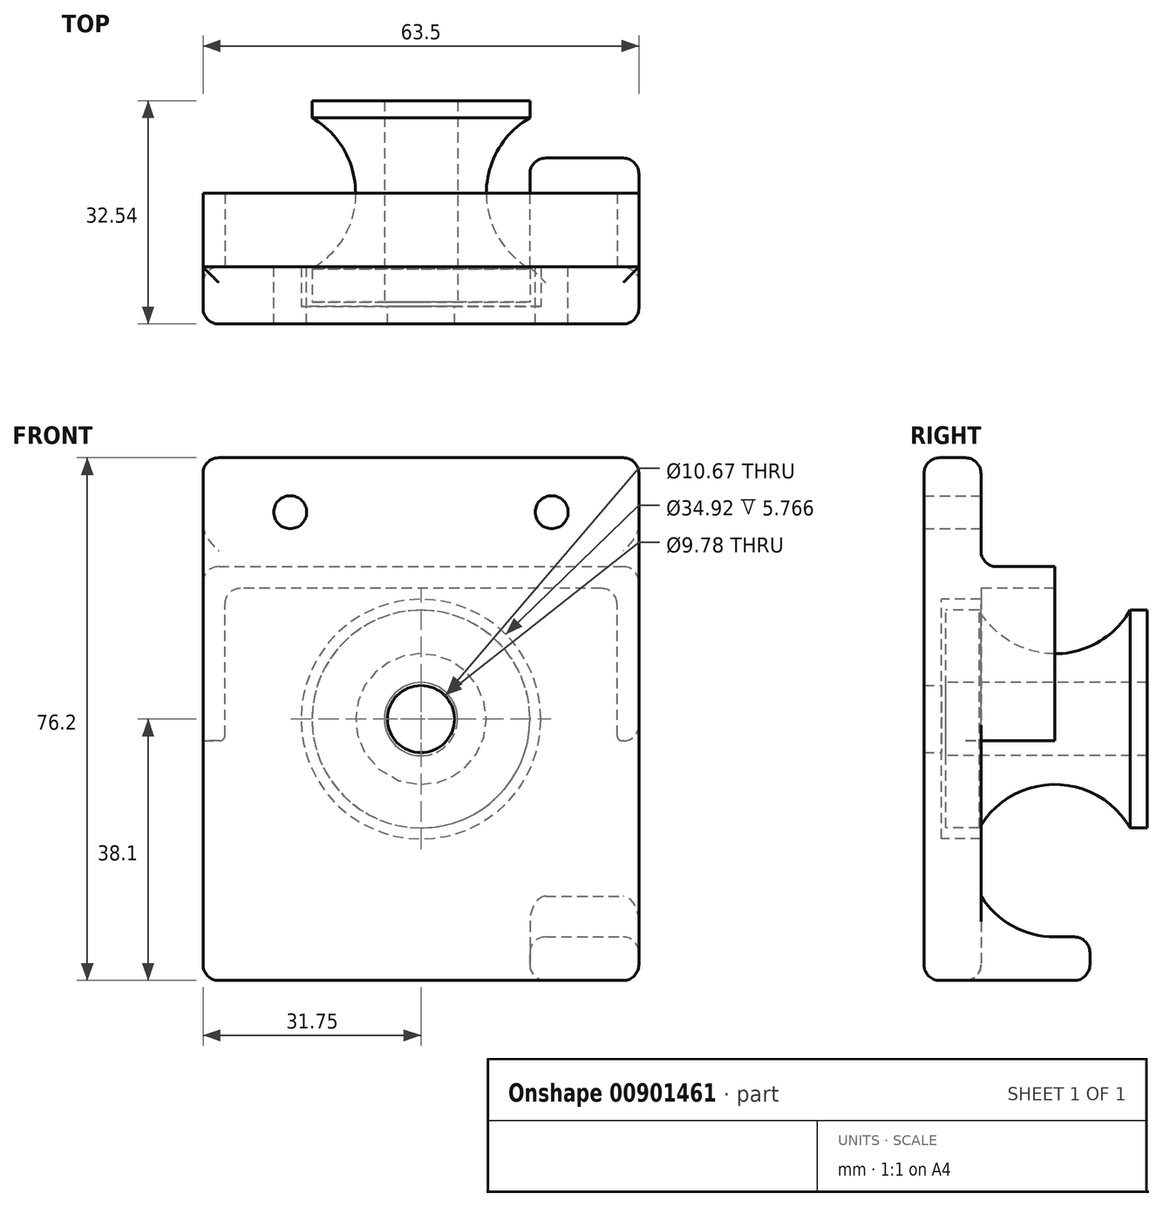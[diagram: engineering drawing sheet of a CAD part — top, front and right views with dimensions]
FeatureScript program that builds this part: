
annotation { "Feature Type Name" : "Feature", "Feature Type Description" : "" }
export const myFeature = defineFeature(function(context is Context, id is Id, definition is map)
    precondition{}
    {
        {
            var Q0;
            Q0=qCreatedBy(makeId("Right.planeOp"),FACE);
            var sketch = newSketch(context, id + "F0", { "sketchPlane" : qUnion([Q0])});
            skLineSegment(sketch, "E0", {"start": v(-15.88, 0) * mm, "end": v(15.88, 0) * mm});
            skLineSegment(sketch, "E1", {"start": v(-15.88, 0) * mm, "end": v(-15.88, 15.88) * mm});
            skArc(sketch, "E2", {"start": v(-11, 15.88) * mm, "mid": v(-6.35, 11.23) * mm, "end": v(0, 9.53) * mm});
            skLineSegment(sketch, "E3", {"start": v(-15.88, 15.88) * mm, "end": v(-11, 15.88) * mm});
            skLineSegment(sketch, "E4", {"start": v(0, 9.53) * mm, "end": v(0, 0) * mm, "construction": true});
            skArc(sketch, "E5.MirrorCS", {"start": v(11, 15.87) * mm, "mid": v(6.35, 11.23) * mm, "end": v(0, 9.53) * mm});
            skLineSegment(sketch, "E6.MirrorCS", {"start": v(15.88, 15.87) * mm, "end": v(11, 15.87) * mm});
            skLineSegment(sketch, "E7.MirrorCS", {"start": v(15.87, 0) * mm, "end": v(15.88, 15.87) * mm});
            skPoint(sketch, "E8.orphan", {"position": v(-16.53, 0) * mm});
            skSolve(sketch);
        }
        {
            var Q0;
            Q0 = qSketchRegion(id + "F0", true);
            var Q1;
            Q1=sQuery(id+"F0.wireOp",EDGE,"E0");
            revolve(context, id + "F1", {"surfaceOperationType" : NewSurfaceOperationType.NEW, "entities" : qUnion([Q0]), "axis" : qUnion([Q1]), "revolveType" : RevolveType.FULL});
        }
        {
            var Q0;
            Q0=makeQuery(id+"F1.opRevolve","SWEPT_FACE",FACE,{"disambiguationData":[OSD([sQuery(id+"F0.wireOp",EDGE,"E1")])]});
            cPlane(context, id + "F2", {"entities" : qUnion([Q0]), "cplaneType" : CPlaneType.OFFSET, "offset" : 0.5 * mm, "width" : 152.4 * mm, "height" : 152.4 * mm});
        }
        {
            var Q0;
            Q0=qCreatedBy(id+"F2.planeOp",FACE);
            var sketch = newSketch(context, id + "F3", { "sketchPlane" : qUnion([Q0])});
            skCircle(sketch, "E9", {"center": v(0, 0) * mm, "radius": 5.33 * mm});
            skSolve(sketch);
        }
        {
            var Q0;
            Q0 = qSketchRegion(id + "F3", true);
            extrude(context, id + "F4", {"entities" : qUnion([Q0]), "operationType" : NewBodyOperationType.REMOVE, "endBound" : BoundingType.THROUGH_ALL, "oppositeDirection" : true, "depth" : 25.4 * mm, "offsetDistance" : 25.4 * mm});
        }
        {
            var Q0;
            Q0=makeQuery(id+"F1.opRevolve","SWEPT_FACE",FACE,{"disambiguationData":[OSD([sQuery(id+"F0.wireOp",EDGE,"E1")])]});
            var sketch = newSketch(context, id + "F5", { "sketchPlane" : qUnion([Q0])});
            skCircle(sketch, "E10", {"center": v(0, 0) * mm, "radius": 17.46 * mm});
            skLineSegment(sketch, "E11.bottom", {"start": v(-31.75, 38.1) * mm, "end": v(31.75, 38.1) * mm});
            skLineSegment(sketch, "E11.top", {"start": v(-31.75, -38.1) * mm, "end": v(31.75, -38.1) * mm});
            skLineSegment(sketch, "E11.left", {"start": v(-31.75, 38.1) * mm, "end": v(-31.75, -38.1) * mm});
            skLineSegment(sketch, "E11.right", {"start": v(31.75, 38.1) * mm, "end": v(31.75, -38.1) * mm});
            skLineSegment(sketch, "E12", {"start": v(-31.75, 0) * mm, "end": v(31.75, 0) * mm, "construction": true});
            skLineSegment(sketch, "E13", {"start": v(0, 38.1) * mm, "end": v(0, -38.1) * mm, "construction": true});
            skSolve(sketch);
        }
        {
            var Q0;
            Q0 = qSketchRegion(id + "F5", true);
            extrude(context, id + "F6", {"entities" : qUnion([Q0]), "oppositeDirection" : true, "depth" : 5.13 * mm, "offsetDistance" : 25.4 * mm, "hasSecondDirection" : true, "secondDirectionOppositeDirection" : false, "secondDirectionDepth" : 3.17 * mm});
        }
        {
            var Q0;
            Q0=makeQuery(id+"F6.opExtrude","CAP_FACE",FACE,{"disambiguationData":[OSD([sQuery(id+"F5.wireOp",EDGE,"E10"),sQuery(id+"F5.wireOp",EDGE,"E11.bottom"),sQuery(id+"F5.wireOp",EDGE,"E11.top"),sQuery(id+"F5.wireOp",EDGE,"E11.left"),sQuery(id+"F5.wireOp",EDGE,"E11.right")])],"isStart":true});
            var sketch = newSketch(context, id + "F7", { "sketchPlane" : qUnion([Q0])});
            skCircle(sketch, "E14.0", {"center": v(0, 0) * mm, "radius": 17.46 * mm});
            skSolve(sketch);
        }
        {
            var Q0;
            Q0 = qSketchRegion(id + "F7", true);
            extrude(context, id + "F8", {"entities" : qUnion([Q0]), "operationType" : NewBodyOperationType.ADD, "oppositeDirection" : true, "depth" : 2.54 * mm, "offsetDistance" : 25.4 * mm});
        }
        {
            var Q0;
            Q0=makeQuery(id+"F6.opExtrude","SWEPT_FACE",FACE,{"disambiguationData":[OSD([sQuery(id+"F5.wireOp",EDGE,"E11.right")])]});
            var sketch = newSketch(context, id + "F9", { "sketchPlane" : qUnion([Q0])});
            skArc(sketch, "E15", {"start": v(-10.74, -25.82) * mm, "mid": v(-6.14, -30.17) * mm, "end": v(0, -31.75) * mm});
            skLineSegment(sketch, "E16", {"start": v(-10.74, -25.82) * mm, "end": v(-10.74, -38.1) * mm});
            skLineSegment(sketch, "E17", {"start": v(-10.74, -38.1) * mm, "end": v(0, -38.1) * mm});
            skLineSegment(sketch, "E18", {"start": v(5.13, -38.1) * mm, "end": v(5.13, -31.75) * mm});
            skLineSegment(sketch, "E19", {"start": v(0, -31.75) * mm, "end": v(5.13, -31.75) * mm});
            skLineSegment(sketch, "E20", {"start": v(0, -38.1) * mm, "end": v(5.13, -38.1) * mm});
            skSolve(sketch);
        }
        {
            var Q0;
            Q0 = qSketchRegion(id + "F9", true);
            extrude(context, id + "F10", {"entities" : qUnion([Q0]), "operationType" : NewBodyOperationType.ADD, "oppositeDirection" : true, "depth" : 15.88 * mm, "offsetDistance" : 25.4 * mm});
        }
        {
            var Q0;
            Q0=makeQuery(id+"F8.opExtrude","CAP_FACE",FACE,{"disambiguationData":[OSD([sQuery(id+"F7.wireOp",EDGE,"E14.0")])],"isStart":false});
            var sketch = newSketch(context, id + "F11", { "sketchPlane" : qUnion([Q0])});
            skCircle(sketch, "E21", {"center": v(0, 0) * mm, "radius": 4.89 * mm});
            skSolve(sketch);
        }
        {
            var Q0;
            Q0 = qSketchRegion(id + "F11", true);
            extrude(context, id + "F12", {"entities" : qUnion([Q0]), "operationType" : NewBodyOperationType.REMOVE, "endBound" : BoundingType.THROUGH_ALL, "oppositeDirection" : true, "depth" : 34.92 * mm, "offsetDistance" : 25.4 * mm});
        }
        {
            var Q0;
            Q0=makeQuery(id+"F6.opExtrude","CAP_FACE",FACE,{"disambiguationData":[OSD([sQuery(id+"F5.wireOp",EDGE,"E10"),sQuery(id+"F5.wireOp",EDGE,"E11.bottom"),sQuery(id+"F5.wireOp",EDGE,"E11.top"),sQuery(id+"F5.wireOp",EDGE,"E11.left"),sQuery(id+"F5.wireOp",EDGE,"E11.right")])],"isStart":false});
            var sketch = newSketch(context, id + "F13", { "sketchPlane" : qUnion([Q0])});
            skLineSegment(sketch, "E22.bottom", {"start": v(-31.75, 22.23) * mm, "end": v(31.75, 22.23) * mm});
            skLineSegment(sketch, "E22.top", {"start": v(-28.58, 19.05) * mm, "end": v(28.57, 19.05) * mm});
            skLineSegment(sketch, "E22.left", {"start": v(-31.75, 22.23) * mm, "end": v(-31.75, 19.05) * mm});
            skLineSegment(sketch, "E22.right", {"start": v(31.75, 22.23) * mm, "end": v(31.75, -3.17) * mm});
            skLineSegment(sketch, "E23", {"start": v(-31.75, 19.05) * mm, "end": v(-31.75, -3.18) * mm});
            skLineSegment(sketch, "E24", {"start": v(-31.75, -3.18) * mm, "end": v(-28.57, -3.18) * mm});
            skLineSegment(sketch, "E25", {"start": v(-28.57, -3.18) * mm, "end": v(-28.57, 19.05) * mm});
            skLineSegment(sketch, "E26", {"start": v(31.75, -3.17) * mm, "end": v(28.57, -3.17) * mm});
            skLineSegment(sketch, "E27", {"start": v(28.57, -3.17) * mm, "end": v(28.57, 19.05) * mm});
            skPoint(sketch, "E28.orphan", {"position": v(31.75, 19.05) * mm});
            skPoint(sketch, "E29.orphan", {"position": v(-31.75, 0) * mm});
            skSolve(sketch);
        }
        {
            var Q0;
            Q0 = qSketchRegion(id + "F13", true);
            var Q1;
            Q1=qCreatedBy(makeId("Front.planeOp"),FACE);
            extrude(context, id + "F14", {"entities" : qUnion([Q0]), "operationType" : NewBodyOperationType.ADD, "endBound" : BoundingType.UP_TO_SURFACE, "depth" : 25.4 * mm, "endBoundEntityFace" : qUnion([Q1]), "offsetDistance" : 25.4 * mm});
        }
        {
            var Q0;
            {var subQ0=sQuery(id+"F5.wireOp",EDGE,"E11.right");var subQ1=sQuery(id+"F5.wireOp",EDGE,"E11.left");var subQ2=sQuery(id+"F5.wireOp",EDGE,"E11.bottom");Q0=makeQuery(id+"F14.boolean.opBoolean","SPLIT",FACE,{"disambiguationData":[TD([makeQuery(id+"F6.opExtrude","SWEPT_FACE",FACE,{"disambiguationData":[OSD([subQ2])]})])],"derivedFrom":makeQuery(id+"F6.opExtrude","CAP_FACE",FACE,{"disambiguationData":[OSD([sQuery(id+"F5.wireOp",EDGE,"E10"),subQ2,sQuery(id+"F5.wireOp",EDGE,"E11.top"),subQ1,subQ0])],"isStart":false})});}
            var sketch = newSketch(context, id + "F15", { "sketchPlane" : qUnion([Q0])});
            skCircle(sketch, "E30", {"center": v(-19.05, 30.16) * mm, "radius": 2.4 * mm});
            skCircle(sketch, "E31", {"center": v(19.05, 30.16) * mm, "radius": 2.4 * mm});
            skLineSegment(sketch, "E32", {"start": v(-19.05, 30.16) * mm, "end": v(19.05, 30.16) * mm, "construction": true});
            skSolve(sketch);
        }
        {
            var Q0;
            Q0 = qSketchRegion(id + "F15", true);
            extrude(context, id + "F16", {"entities" : qUnion([Q0]), "operationType" : NewBodyOperationType.REMOVE, "endBound" : BoundingType.THROUGH_ALL, "oppositeDirection" : true, "depth" : 25.4 * mm, "offsetDistance" : 25.4 * mm});
        }
        {
            var Q0;
            Q0=makeQuery(id+"F14.opExtrude","SWEPT_EDGE",EDGE,{"disambiguationData":[OSD([sQuery(id+"F13.wireOp",EDGE,"E22.top"),sQuery(id+"F13.wireOp",EDGE,"E25")])]});
            var Q1;
            Q1=makeQuery(id+"F14.opExtrude","SWEPT_EDGE",EDGE,{"disambiguationData":[OSD([sQuery(id+"F13.wireOp",EDGE,"E22.top"),sQuery(id+"F13.wireOp",EDGE,"E27")])]});
            var Q2;
            Q2=makeQuery(id+"F10.opExtrude","CAP_EDGE",EDGE,{"disambiguationData":[OSD([sQuery(id+"F9.wireOp",EDGE,"E15")])],"isStart":true});
            var Q3;
            Q3=makeQuery(id+"F10.opExtrude","CAP_EDGE",EDGE,{"disambiguationData":[OSD([sQuery(id+"F9.wireOp",EDGE,"E15")])],"isStart":false});
            var Q4;
            Q4=makeQuery(id+"F10.opExtrude","SWEPT_FACE",FACE,{"disambiguationData":[OSD([sQuery(id+"F9.wireOp",EDGE,"E18")])]});
            var Q5;
            Q5=makeQuery(id+"F10.boolean.opBoolean","MERGE",EDGE,{"derivedFrom":[makeQuery(id+"F6.opExtrude","SWEPT_EDGE",EDGE,{"disambiguationData":[OSD([sQuery(id+"F5.wireOp",EDGE,"E11.top"),sQuery(id+"F5.wireOp",EDGE,"E11.right")])]}),makeQuery(id+"F10.opExtrude","CAP_EDGE",EDGE,{"disambiguationData":[OSD([sQuery(id+"F9.wireOp",EDGE,"E17"),sQuery(id+"F9.wireOp",EDGE,"E20")])],"isStart":true})]});
            var Q6;
            Q6=makeQuery(id+"F10.opExtrude","CAP_EDGE",EDGE,{"disambiguationData":[OSD([sQuery(id+"F9.wireOp",EDGE,"E17"),sQuery(id+"F9.wireOp",EDGE,"E20")])],"isStart":false});
            var Q7;
            Q7=makeQuery(id+"F6.opExtrude","CAP_EDGE",EDGE,{"disambiguationData":[OSD([sQuery(id+"F5.wireOp",EDGE,"E11.top")])],"isStart":false});
            var Q8;
            Q8=makeQuery(id+"F6.opExtrude","CAP_EDGE",EDGE,{"disambiguationData":[OSD([sQuery(id+"F5.wireOp",EDGE,"E11.top")])],"isStart":true});
            var Q9;
            Q9=makeQuery(id+"F6.opExtrude","SWEPT_FACE",FACE,{"disambiguationData":[OSD([sQuery(id+"F5.wireOp",EDGE,"E11.bottom")])]});
            var Q10;
            Q10=makeQuery(id+"F14.opExtrude","CAP_EDGE",EDGE,{"disambiguationData":[OSD([sQuery(id+"F13.wireOp",EDGE,"E22.bottom")])],"isStart":true});
            var Q11;
            Q11=makeQuery(id+"F14.opExtrude","CAP_EDGE",EDGE,{"disambiguationData":[OSD([sQuery(id+"F13.wireOp",EDGE,"E22.top")])],"isStart":true});
            var Q12;
            Q12=makeQuery(id+"F14.opExtrude","CAP_EDGE",EDGE,{"disambiguationData":[OSD([sQuery(id+"F13.wireOp",EDGE,"E25")])],"isStart":true});
            var Q13;
            Q13=makeQuery(id+"F14.opExtrude","CAP_EDGE",EDGE,{"disambiguationData":[OSD([sQuery(id+"F13.wireOp",EDGE,"E27")])],"isStart":true});
            var Q14;
            Q14=makeQuery(id+"F14.opExtrude","CAP_EDGE",EDGE,{"disambiguationData":[OSD([sQuery(id+"F13.wireOp",EDGE,"E26")])],"isStart":true});
            var Q15;
            {var subQ0=sQuery(id+"F5.wireOp",EDGE,"E11.left");var subQ1=sQuery(id+"F5.wireOp",EDGE,"E11.top");Q15=makeQuery(id+"F14.boolean.opBoolean","SPLIT",EDGE,{"disambiguationData":[TD([makeQuery(id+"F6.opExtrude","SWEPT_FACE",FACE,{"disambiguationData":[OSD([subQ1])]})])],"derivedFrom":makeQuery(id+"F6.opExtrude","CAP_EDGE",EDGE,{"disambiguationData":[OSD([subQ0])],"isStart":false})});}
            var Q16;
            Q16=makeQuery(id+"F6.opExtrude","SWEPT_EDGE",EDGE,{"disambiguationData":[OSD([sQuery(id+"F5.wireOp",EDGE,"E11.top"),sQuery(id+"F5.wireOp",EDGE,"E11.left")])]});
            var Q17;
            Q17=makeQuery(id+"F6.opExtrude","CAP_EDGE",EDGE,{"disambiguationData":[OSD([sQuery(id+"F5.wireOp",EDGE,"E11.left")])],"isStart":true});
            var Q18;
            Q18=makeQuery(id+"F14.opExtrude","SWEPT_EDGE",EDGE,{"disambiguationData":[OSD([sQuery(id+"F5.wireOp",EDGE,"E11.left"),sQuery(id+"F13.wireOp",EDGE,"E22.bottom"),sQuery(id+"F13.wireOp",EDGE,"E22.right")])]});
            var Q19;
            Q19=makeQuery(id+"F14.opExtrude","CAP_EDGE",EDGE,{"disambiguationData":[OSD([sQuery(id+"F13.wireOp",EDGE,"E24")])],"isStart":true});
            var Q20;
            Q20=makeQuery(id+"F14.opExtrude","SWEPT_EDGE",EDGE,{"disambiguationData":[OSD([sQuery(id+"F5.wireOp",EDGE,"E11.right"),sQuery(id+"F13.wireOp",EDGE,"E23"),sQuery(id+"F13.wireOp",EDGE,"E24")])]});
            var Q21;
            Q21=makeQuery(id+"F14.opExtrude","SWEPT_EDGE",EDGE,{"disambiguationData":[OSD([sQuery(id+"F5.wireOp",EDGE,"E11.right"),sQuery(id+"F13.wireOp",EDGE,"E22.bottom"),sQuery(id+"F13.wireOp",EDGE,"E22.left")])]});
            var Q22;
            Q22=makeQuery(id+"F6.opExtrude","CAP_EDGE",EDGE,{"disambiguationData":[OSD([sQuery(id+"F5.wireOp",EDGE,"E11.right")])],"isStart":true});
            fillet(context, id + "F17", {"entities" : qUnion([Q0, Q1, Q2, Q3, Q4, Q5, Q6, Q7, Q8, Q9, Q10, Q11, Q12, Q13, Q14, Q15, Q16, Q17, Q18, Q19, Q20, Q21, Q22]), "radius" : 2.3 * mm, "tangentPropagation" : true, "allowEdgeOverflow" : false});
        }
        {
            var Q0;
            Q0=makeQuery(id+"F14.opExtrude","SWEPT_EDGE",EDGE,{"disambiguationData":[OSD([sQuery(id+"F13.wireOp",EDGE,"E24"),sQuery(id+"F13.wireOp",EDGE,"E25")])]});
            var Q1;
            Q1=makeQuery(id+"F14.opExtrude","SWEPT_EDGE",EDGE,{"disambiguationData":[OSD([sQuery(id+"F13.wireOp",EDGE,"E26"),sQuery(id+"F13.wireOp",EDGE,"E27")])]});
            fillet(context, id + "F18", {"entities" : qUnion([Q0, Q1]), "radius" : 0.76 * mm, "tangentPropagation" : true, "allowEdgeOverflow" : false});
        }
        {
            var Q0;
            Q0=qCreatedBy(makeId("Right.planeOp"),FACE);
            var sketch = newSketch(context, id + "F19", { "sketchPlane" : qUnion([Q0])});
            skLineSegment(sketch, "E33.bottom", {"start": v(13.49, 36.6) * mm, "end": v(21.12, 36.6) * mm});
            skLineSegment(sketch, "E33.top", {"start": v(13.49, -33.71) * mm, "end": v(21.12, -33.71) * mm});
            skLineSegment(sketch, "E33.left", {"start": v(13.49, 36.6) * mm, "end": v(13.49, -33.71) * mm});
            skLineSegment(sketch, "E33.right", {"start": v(21.12, 36.6) * mm, "end": v(21.12, -33.71) * mm});
            skSolve(sketch);
        }
        {
            var Q0;
            Q0 = qSketchRegion(id + "F19", true);
            extrude(context, id + "F20", {"entities" : qUnion([Q0]), "operationType" : NewBodyOperationType.REMOVE, "endBound" : BoundingType.SYMMETRIC, "depth" : 38.1 * mm, "offsetDistance" : 25.4 * mm});
        }
    });
